# Revit family: ORBR
name_source: partatom
category: Mechanical Equipment
units: mm (PartAtom-declared; Revit-internal decimal feet)

## family parameters
Always vertical = Yes
Cut with Voids When Loaded = No
OmniClass Number = 23.40.40.11.17
OmniClass Title = Refrigerated Cases
Part Type = Normal
Room Calculation Point = No
Round Connector Dimension = Use Radius
Shared = No
Work Plane-Based = Yes

## types (4) — shared parameters
27" Shelf = Yes
ANTI SWEAT APPARENT LOAD = 0 VA
Application Discipline = Beverage
Certifications = NSF 7, UL471, CSA
DATE = 02/19/2016
Default Elevation = 48"
Defrosts Per Day_2 = 4
Description = Reach-In Rear Load Merchandiser
Discharge Air (°F) = 38° F
Discharge Air Velocity (FPM) = 380 (FPM)
EQUIPMENT DESCRIPTION = Reach-In Rear Load Merchandiser
EQUIPMENT MARK = ORBR
Evaporator (°F) = 34° F
GLASS = Glass
Height = 81 1/4"
High Efficiency Amps = 1 A
Item Description = Reach-In Rear Load Merchandiser
Keynote = ORBR
Legend Number = ORBR
Manufacturer = HILL PHOENIX
Model = ORBR
PAINTED METAL UPPER SHELF = PAINTED SHELVES
REFRIGERATION PIPING = COPPER PIPE
STAINLESS STEEL = GALVANIZED STEEL
Superheat Set Point @ Bulb (°F) = 6-8° F
TIMED OFF DEFROST FAIL-SAFE (Min) = 30
TIMED OFF DEFROST TERMINATION TEMP = 40 °F
Timed-Off Defrost Fail-Safe (Min) = 30 (Min)
Timed-Off Defrost Termination Temp_2 = 47° F
URL = http://www.hillphoenix.com
Width = 44 1/8"
back door one = Yes
back door two = Yes

## per-type parameters (varying)
- 08'-24"-Door-Beverage: 101 Amps=0 A; 101 Watts=47 W; BTUH Conventional=718; BTUH Parallel=678; CENTER LINE & DRAIN=48"; Crossfire/Polaris Amps=0 A; Crossfire/Polaris Watts=0 W; DOOR CONFIGURATION=MASTER DOOR : 24" X 64 3/8" 4 DOOR B SWING; Door=24 x 64 - 8' & 12' door : 24 x 64 - 8'; Eliminaator Amps=0 A; Eliminaator Watts=47 W; GE Immersion Amps=0 A; GE Immersion Watts=0 W; High Efficiency Watts=78 W; Length=96"; Length of Cases=96"; NUMBER FOR ELECTRICAL DATA=1; NUMBER FOR GUIDLINES AND CONTROL ORGANIZATION=1; NUMBER FOR LIGHTING DATA=1; NUMBER OF DOORS=4; Number of Fans per Case=3; Optimax Pro Amps=1 A; Optimax Pro Watts=87 W; Size of Door=24"; Type of Door Swing=B-Swing; Vista-C/60 Amps=1 A; Vista-C/60 Watts=70 W; back door three=No
- 08'-32"-Door-Beverage: 101 Amps=1 A; 101 Watts=61 W; BTUH Conventional=957; BTUH Parallel=904; CENTER LINE & DRAIN=48"; Crossfire/Polaris Amps=0 A; Crossfire/Polaris Watts=45 W; DOOR CONFIGURATION=MASTER DOOR : 32" X 64 3/8" 3 DOOR B SWING (LEFT OPENING END); Door=24 x 64 - 8' & 12' door : 24 x 64 - 8'; Eliminaator Amps=1 A; Eliminaator Watts=61 W; GE Immersion Amps=0 A; GE Immersion Watts=48 W; High Efficiency Watts=78 W; Length=96"; Length of Cases=96"; NUMBER FOR ELECTRICAL DATA=1; NUMBER FOR GUIDLINES AND CONTROL ORGANIZATION=3; NUMBER FOR LIGHTING DATA=2; NUMBER OF DOORS=3; Number of Fans per Case=3; Optimax Pro Amps=0 A; Optimax Pro Watts=58 W; Size of Door=32"; Type of Door Swing=A-Swing; Vista-C/60 Amps=0 A; Vista-C/60 Watts=0 W; back door three=No
- 12'-24"-Door-Beverage: 101 Amps=1 A; 101 Watts=76 W; BTUH Conventional=718; BTUH Parallel=678; CENTER LINE & DRAIN=72"; Crossfire/Polaris Amps=0 A; Crossfire/Polaris Watts=0 W; DOOR CONFIGURATION=MASTER DOOR : 24" X 64 3/8" 6 DOOR B SWING; Door=24 x 64 - 8' & 12' door : 24 x 64 - 12'; Eliminaator Amps=1 A; Eliminaator Watts=76 W; GE Immersion Amps=0 A; GE Immersion Watts=0 W; High Efficiency Watts=104 W; Length=144"; Length of Cases=144"; NUMBER FOR ELECTRICAL DATA=2; NUMBER FOR GUIDLINES AND CONTROL ORGANIZATION=2; NUMBER FOR LIGHTING DATA=3; NUMBER OF DOORS=6; Number of Fans per Case=4; Optimax Pro Amps=1 A; Optimax Pro Watts=130 W; Size of Door=24"; Type of Door Swing=B-Swing; Vista-C/60 Amps=1 A; Vista-C/60 Watts=94 W; back door three=Yes
- 12'-36"-Door-Beverage: 101 Amps=1 A; 101 Watts=89 W; BTUH Conventional=1071; BTUH Parallel=1017; CENTER LINE & DRAIN=72"; Crossfire/Polaris Amps=1 A; Crossfire/Polaris Watts=60 W; DOOR CONFIGURATION=MASTER DOOR : 36" X 64 3/8" 4 DOOR B SWING; Door=24 x 64 - 8' & 12' door : 24 x 64 - 8'; Eliminaator Amps=1 A; Eliminaator Watts=89 W; GE Immersion Amps=1 A; GE Immersion Watts=64 W; High Efficiency Watts=104 W; Length=144"; Length of Cases=144"; NUMBER FOR ELECTRICAL DATA=0; NUMBER FOR GUIDLINES AND CONTROL ORGANIZATION=3; NUMBER FOR LIGHTING DATA=4; NUMBER OF DOORS=4; Number of Fans per Case=4; Optimax Pro Amps=1 A; Optimax Pro Watts=77 W; Size of Door=36"; Type of Door Swing=B-Swing; Vista-C/60 Amps=0 A; Vista-C/60 Watts=0 W; back door three=Yes

## geometry (parser evidence)
native form markers: Blend x8, Sweep x32
no freeform markers — native parametric forms only
